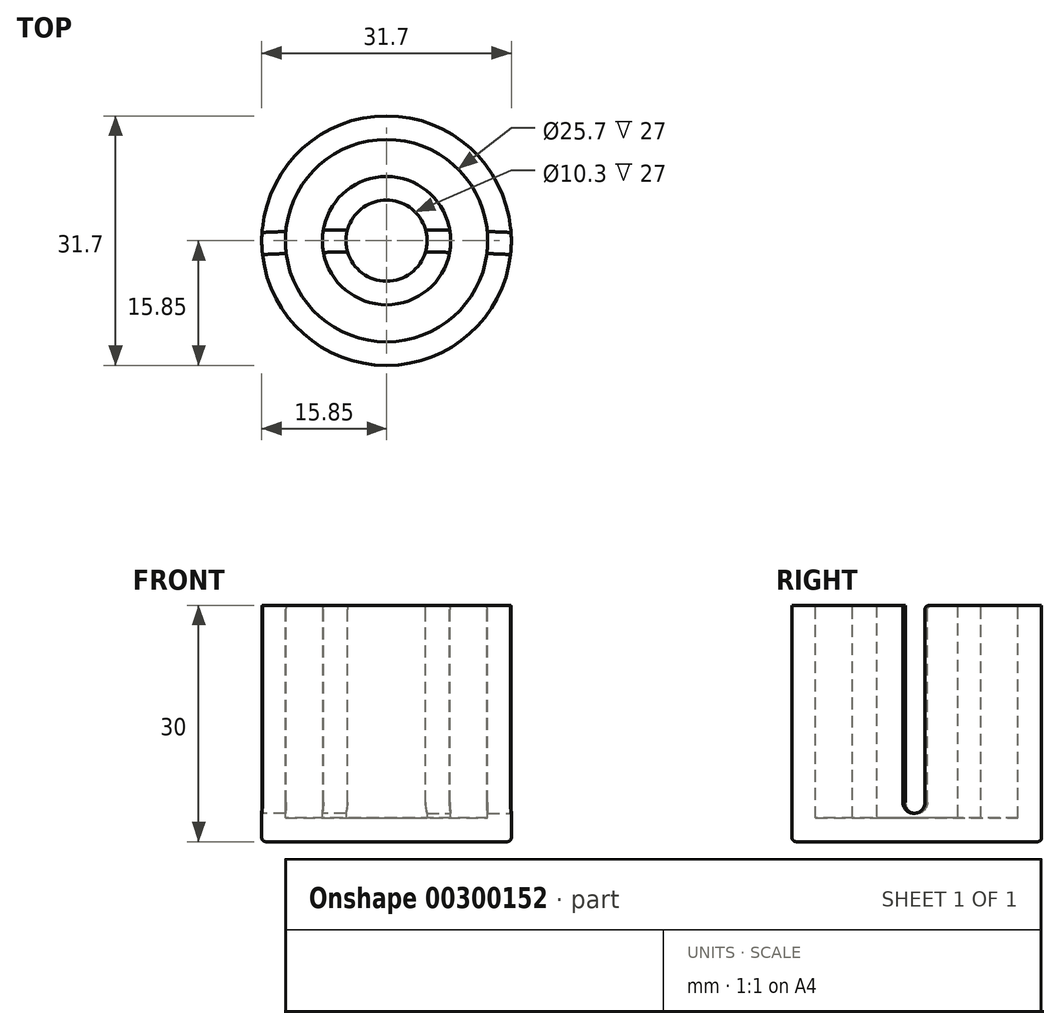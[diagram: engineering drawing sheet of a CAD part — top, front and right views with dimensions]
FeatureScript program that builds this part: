
annotation { "Feature Type Name" : "Feature", "Feature Type Description" : "" }
export const myFeature = defineFeature(function(context is Context, id is Id, definition is map)
    precondition{}
    {
        {
            var Q0;
            Q0=qCreatedBy(makeId("Top.planeOp"),FACE);
            var sketch = newSketch(context, id + "F0", { "sketchPlane" : qUnion([Q0])});
            skCircle(sketch, "E0", {"center": v(0, 0) * mm, "radius": 15.85 * mm});
            skCircle(sketch, "E1", {"center": v(0, 0) * mm, "radius": 5.15 * mm});
            skSolve(sketch);
        }
        {
            var Q0;
            Q0=qSketchRegion(id+"F0",true);
            extrude(context, id + "F1", {"entities" : qUnion([Q0]), "depth" : 30 * mm});
        }
        {
            var Q0;
            Q0=makeQuery(id+"F1.opExtrude","CAP_FACE",FACE,{"disambiguationData":[OSD([sQuery(id+"F0.wireOp",EDGE,"E0"),sQuery(id+"F0.wireOp",EDGE,"E1")])],"isStart":false});
            var sketch = newSketch(context, id + "F2", { "sketchPlane" : qUnion([Q0])});
            skCircle(sketch, "E2", {"center": v(0, 0) * mm, "radius": 12.85 * mm});
            skCircle(sketch, "E3", {"center": v(0, 0) * mm, "radius": 8.15 * mm});
            skSolve(sketch);
        }
        {
            var Q0;
            Q0=qSketchRegion(id+"F2",true);
            extrude(context, id + "F3", {"entities" : qUnion([Q0]), "operationType" : NewBodyOperationType.REMOVE, "oppositeDirection" : true, "depth" : 40 * mm});
        }
        {
            var Q0;
            Q0=makeQuery(id+"F1.opExtrude","CAP_FACE",FACE,{"disambiguationData":[OSD([sQuery(id+"F0.wireOp",EDGE,"E0"),sQuery(id+"F0.wireOp",EDGE,"E1")])],"isStart":true});
            var sketch = newSketch(context, id + "F4", { "sketchPlane" : qUnion([Q0])});
            skCircle(sketch, "E4", {"center": v(0, 0) * mm, "radius": 8.9 * mm});
            skCircle(sketch, "E5", {"center": v(0, 0) * mm, "radius": 12.65 * mm});
            skSolve(sketch);
        }
        {
            var Q0;
            Q0=qSketchRegion(id+"F4",true);
            extrude(context, id + "F5", {"entities" : qUnion([Q0]), "operationType" : NewBodyOperationType.REMOVE, "oppositeDirection" : true, "depth" : 40 * mm});
        }
        {
            var Q0;
            {var subQ0=sQuery(id+"F0.wireOp",EDGE,"E1");Q0=makeQuery(id+"F3.boolean.opBoolean","SPLIT",FACE,{"disambiguationData":[TD([makeQuery(id+"F1.opExtrude","SWEPT_FACE",FACE,{"disambiguationData":[OSD([subQ0])]})])],"derivedFrom":makeQuery(id+"F1.opExtrude","CAP_FACE",FACE,{"disambiguationData":[OSD([sQuery(id+"F0.wireOp",EDGE,"E0"),subQ0])],"isStart":false})});}
            var sketch = newSketch(context, id + "F6", { "sketchPlane" : qUnion([Q0])});
            skCircle(sketch, "E6", {"center": v(0, -340) * mm, "radius": 340 * mm, "construction": true});
            skPoint(sketch, "E7", {"position": v(0, 0) * mm});
            skSolve(sketch);
        }
        {
            var Q0;
            Q0=qCreatedBy(makeId("Right.planeOp"),FACE);
            var sketch = newSketch(context, id + "F7", { "sketchPlane" : qUnion([Q0])});
            skLineSegment(sketch, "E8", {"start": v(1.4, 30) * mm, "end": v(0, 30) * mm});
            skArc(sketch, "E9", {"start": v(0, 3.6) * mm, "mid": v(0.99, 4.01) * mm, "end": v(1.4, 5) * mm});
            skArc(sketch, "E10.MirrorCS", {"start": v(0, 3.6) * mm, "mid": v(-0.99, 4.01) * mm, "end": v(-1.4, 5) * mm});
            skLineSegment(sketch, "E11", {"start": v(0, 30) * mm, "end": v(-1.4, 30) * mm});
            skLineSegment(sketch, "E12", {"start": v(-1.4, 30) * mm, "end": v(-1.4, 5) * mm});
            skLineSegment(sketch, "E13", {"start": v(1.4, 5) * mm, "end": v(1.4, 30) * mm});
            skSolve(sketch);
        }
        {
            var Q0;
            Q0=qCreatedBy(makeId("Right.planeOp"),FACE);
            var sketch = newSketch(context, id + "F8", { "sketchPlane" : qUnion([Q0])});
            skLineSegment(sketch, "E14", {"start": v(-340, -124.57) * mm, "end": v(-340, 184) * mm, "construction": true});
            skSolve(sketch);
        }
        {
            var Q0;
            Q0=qSketchRegion(id+"F7",true);
            var Q1;
            Q1=sQuery(id+"F8.wireOp",EDGE,"E14");
            revolve(context, id + "F9", {"operationType" : NewBodyOperationType.REMOVE, "entities" : qUnion([Q0]), "axis" : qUnion([Q1]), "revolveType" : RevolveType.FULL, "oppositeDirection" : true});
        }
        {
            var Q0;
            {var subQ0=sQuery(id+"F0.wireOp",EDGE,"E0");Q0=makeQuery(id+"F9.boolean.opBoolean","SPLIT",EDGE,{"disambiguationData":[TD([makeQuery(id+"F9.opRevolve","SWEPT_FACE",FACE,{"disambiguationData":[OSD([sQuery(id+"F7.wireOp",EDGE,"EXb8YkG8-jNmO-N3WI-U9VX-eYOkCgfbIMvW")])]})])],"derivedFrom":makeQuery(id+"F1.opExtrude","CAP_EDGE",EDGE,{"disambiguationData":[OSD([subQ0])],"isStart":false})});}
            var Q1;
            {var subQ0=sQuery(id+"F2.wireOp",EDGE,"E2");Q1=makeQuery(id+"F9.boolean.opBoolean","SPLIT",EDGE,{"disambiguationData":[TD([makeQuery(id+"F9.opRevolve","SWEPT_FACE",FACE,{"disambiguationData":[OSD([sQuery(id+"F7.wireOp",EDGE,"EXb8YkG8-jNmO-N3WI-U9VX-eYOkCgfbIMvW")])]})])],"derivedFrom":makeQuery(id+"F3.boolean.opBoolean","COPY",EDGE,{"derivedFrom":makeQuery(id+"F3.opExtrude","CAP_EDGE",EDGE,{"disambiguationData":[OSD([subQ0])],"isStart":true})})});}
            var Q2;
            Q2=makeQuery(id+"F9.boolean.opBoolean","INTERSECT",EDGE,{"disambiguationData":[OD(0.0)],"derivedFrom":[makeQuery(id+"F1.opExtrude","SWEPT_FACE",FACE,{"disambiguationData":[OSD([sQuery(id+"F0.wireOp",EDGE,"E0")])]}),makeQuery(id+"F9.opRevolve","SWEPT_FACE",FACE,{"disambiguationData":[OSD([sQuery(id+"F7.wireOp",EDGE,"EXb8YkG8-jNmO-N3WI-U9VX-eYOkCgfbIMvW")])]})]});
            var Q3;
            {var subQ0=sQuery(id+"F0.wireOp",EDGE,"E0");var subQ1=sQuery(id+"F7.wireOp",EDGE,"EXb8YkG8-jNmO-N3WI-U9VX-eYOkCgfbIMvW");Q3=makeQuery(id+"F9.boolean.opBoolean","COPY",EDGE,{"disambiguationData":[TD([makeQuery(id+"F1.opExtrude","SWEPT_FACE",FACE,{"disambiguationData":[OSD([subQ0])]}),makeQuery(id+"F1.opExtrude","CAP_FACE",FACE,{"disambiguationData":[OSD([subQ0,sQuery(id+"F0.wireOp",EDGE,"E1")])],"isStart":false}),makeQuery(id+"F3.boolean.opBoolean","COPY",FACE,{"derivedFrom":makeQuery(id+"F3.opExtrude","SWEPT_FACE",FACE,{"disambiguationData":[OSD([sQuery(id+"F2.wireOp",EDGE,"E2")])]})}),makeQuery(id+"F9.opRevolve","SWEPT_FACE",FACE,{"disambiguationData":[OSD([subQ1])]})]),OD(0.0)],"derivedFrom":makeQuery(id+"F9.opRevolve","SWEPT_EDGE",EDGE,{"disambiguationData":[OSD([sQuery(id+"F7.wireOp",EDGE,"E8"),subQ1])]})});}
            var Q4;
            {var subQ0=sQuery(id+"F0.wireOp",EDGE,"E0");var subQ1=sQuery(id+"F7.wireOp",EDGE,"b1084e50-73aa-409a-998b-8d194c50b8df0.MirrorCS");Q4=makeQuery(id+"F9.boolean.opBoolean","COPY",EDGE,{"disambiguationData":[TD([makeQuery(id+"F1.opExtrude","SWEPT_FACE",FACE,{"disambiguationData":[OSD([subQ0])]}),makeQuery(id+"F1.opExtrude","CAP_FACE",FACE,{"disambiguationData":[OSD([subQ0,sQuery(id+"F0.wireOp",EDGE,"E1")])],"isStart":false}),makeQuery(id+"F3.boolean.opBoolean","COPY",FACE,{"derivedFrom":makeQuery(id+"F3.opExtrude","SWEPT_FACE",FACE,{"disambiguationData":[OSD([sQuery(id+"F2.wireOp",EDGE,"E2")])]})}),makeQuery(id+"F9.opRevolve","SWEPT_FACE",FACE,{"disambiguationData":[OSD([subQ1])]})]),OD(0.0)],"derivedFrom":makeQuery(id+"F9.opRevolve","SWEPT_EDGE",EDGE,{"disambiguationData":[OSD([subQ1,sQuery(id+"F7.wireOp",EDGE,"E11")])]})});}
            var Q5;
            {var subQ0=sQuery(id+"F0.wireOp",EDGE,"E0");Q5=makeQuery(id+"F9.boolean.opBoolean","SPLIT",EDGE,{"disambiguationData":[TD([makeQuery(id+"F9.opRevolve","SWEPT_FACE",FACE,{"disambiguationData":[OSD([sQuery(id+"F7.wireOp",EDGE,"b1084e50-73aa-409a-998b-8d194c50b8df0.MirrorCS")])]})])],"derivedFrom":makeQuery(id+"F1.opExtrude","CAP_EDGE",EDGE,{"disambiguationData":[OSD([subQ0])],"isStart":false})});}
            var Q6;
            {var subQ0=sQuery(id+"F2.wireOp",EDGE,"E2");Q6=makeQuery(id+"F9.boolean.opBoolean","SPLIT",EDGE,{"disambiguationData":[TD([makeQuery(id+"F9.opRevolve","SWEPT_FACE",FACE,{"disambiguationData":[OSD([sQuery(id+"F7.wireOp",EDGE,"b1084e50-73aa-409a-998b-8d194c50b8df0.MirrorCS")])]})])],"derivedFrom":makeQuery(id+"F3.boolean.opBoolean","COPY",EDGE,{"derivedFrom":makeQuery(id+"F3.opExtrude","CAP_EDGE",EDGE,{"disambiguationData":[OSD([subQ0])],"isStart":true})})});}
            var Q7;
            Q7=makeQuery(id+"F9.boolean.opBoolean","INTERSECT",EDGE,{"disambiguationData":[OD(0.0)],"derivedFrom":[makeQuery(id+"F3.boolean.opBoolean","COPY",FACE,{"derivedFrom":makeQuery(id+"F3.opExtrude","SWEPT_FACE",FACE,{"disambiguationData":[OSD([sQuery(id+"F2.wireOp",EDGE,"E2")])]})}),makeQuery(id+"F9.opRevolve","SWEPT_FACE",FACE,{"disambiguationData":[OSD([sQuery(id+"F7.wireOp",EDGE,"EXb8YkG8-jNmO-N3WI-U9VX-eYOkCgfbIMvW")])]})]});
            var Q8;
            Q8=makeQuery(id+"F9.boolean.opBoolean","INTERSECT",EDGE,{"disambiguationData":[OD(1.0)],"derivedFrom":[makeQuery(id+"F1.opExtrude","SWEPT_FACE",FACE,{"disambiguationData":[OSD([sQuery(id+"F0.wireOp",EDGE,"E0")])]}),makeQuery(id+"F9.opRevolve","SWEPT_FACE",FACE,{"disambiguationData":[OSD([sQuery(id+"F7.wireOp",EDGE,"EXb8YkG8-jNmO-N3WI-U9VX-eYOkCgfbIMvW")])]})]});
            var Q9;
            Q9=makeQuery(id+"F9.boolean.opBoolean","INTERSECT",EDGE,{"disambiguationData":[OD(1.0)],"derivedFrom":[makeQuery(id+"F3.boolean.opBoolean","COPY",FACE,{"derivedFrom":makeQuery(id+"F3.opExtrude","SWEPT_FACE",FACE,{"disambiguationData":[OSD([sQuery(id+"F2.wireOp",EDGE,"E2")])]})}),makeQuery(id+"F9.opRevolve","SWEPT_FACE",FACE,{"disambiguationData":[OSD([sQuery(id+"F7.wireOp",EDGE,"EXb8YkG8-jNmO-N3WI-U9VX-eYOkCgfbIMvW")])]})]});
            var Q10;
            {var subQ0=sQuery(id+"F0.wireOp",EDGE,"E0");var subQ1=sQuery(id+"F7.wireOp",EDGE,"EXb8YkG8-jNmO-N3WI-U9VX-eYOkCgfbIMvW");Q10=makeQuery(id+"F9.boolean.opBoolean","COPY",EDGE,{"disambiguationData":[TD([makeQuery(id+"F1.opExtrude","SWEPT_FACE",FACE,{"disambiguationData":[OSD([subQ0])]}),makeQuery(id+"F1.opExtrude","CAP_FACE",FACE,{"disambiguationData":[OSD([subQ0,sQuery(id+"F0.wireOp",EDGE,"E1")])],"isStart":false}),makeQuery(id+"F3.boolean.opBoolean","COPY",FACE,{"derivedFrom":makeQuery(id+"F3.opExtrude","SWEPT_FACE",FACE,{"disambiguationData":[OSD([sQuery(id+"F2.wireOp",EDGE,"E2")])]})}),makeQuery(id+"F9.opRevolve","SWEPT_FACE",FACE,{"disambiguationData":[OSD([subQ1])]})]),OD(1.0)],"derivedFrom":makeQuery(id+"F9.opRevolve","SWEPT_EDGE",EDGE,{"disambiguationData":[OSD([sQuery(id+"F7.wireOp",EDGE,"E8"),subQ1])]})});}
            var Q11;
            {var subQ0=sQuery(id+"F0.wireOp",EDGE,"E0");var subQ1=sQuery(id+"F7.wireOp",EDGE,"b1084e50-73aa-409a-998b-8d194c50b8df0.MirrorCS");Q11=makeQuery(id+"F9.boolean.opBoolean","COPY",EDGE,{"disambiguationData":[TD([makeQuery(id+"F1.opExtrude","SWEPT_FACE",FACE,{"disambiguationData":[OSD([subQ0])]}),makeQuery(id+"F1.opExtrude","CAP_FACE",FACE,{"disambiguationData":[OSD([subQ0,sQuery(id+"F0.wireOp",EDGE,"E1")])],"isStart":false}),makeQuery(id+"F3.boolean.opBoolean","COPY",FACE,{"derivedFrom":makeQuery(id+"F3.opExtrude","SWEPT_FACE",FACE,{"disambiguationData":[OSD([sQuery(id+"F2.wireOp",EDGE,"E2")])]})}),makeQuery(id+"F9.opRevolve","SWEPT_FACE",FACE,{"disambiguationData":[OSD([subQ1])]})]),OD(1.0)],"derivedFrom":makeQuery(id+"F9.opRevolve","SWEPT_EDGE",EDGE,{"disambiguationData":[OSD([subQ1,sQuery(id+"F7.wireOp",EDGE,"E11")])]})});}
            var Q12;
            {var subQ0=sQuery(id+"F2.wireOp",EDGE,"E3");Q12=makeQuery(id+"F9.boolean.opBoolean","SPLIT",EDGE,{"disambiguationData":[TD([makeQuery(id+"F9.opRevolve","SWEPT_FACE",FACE,{"disambiguationData":[OSD([sQuery(id+"F7.wireOp",EDGE,"b1084e50-73aa-409a-998b-8d194c50b8df0.MirrorCS")])]})])],"derivedFrom":makeQuery(id+"F3.boolean.opBoolean","COPY",EDGE,{"derivedFrom":makeQuery(id+"F3.opExtrude","CAP_EDGE",EDGE,{"disambiguationData":[OSD([subQ0])],"isStart":true})})});}
            var Q13;
            {var subQ0=sQuery(id+"F0.wireOp",EDGE,"E1");var subQ1=sQuery(id+"F7.wireOp",EDGE,"b1084e50-73aa-409a-998b-8d194c50b8df0.MirrorCS");Q13=makeQuery(id+"F9.boolean.opBoolean","COPY",EDGE,{"disambiguationData":[TD([makeQuery(id+"F1.opExtrude","CAP_FACE",FACE,{"disambiguationData":[OSD([sQuery(id+"F0.wireOp",EDGE,"E0"),subQ0])],"isStart":false}),makeQuery(id+"F1.opExtrude","SWEPT_FACE",FACE,{"disambiguationData":[OSD([subQ0])]}),makeQuery(id+"F3.boolean.opBoolean","COPY",FACE,{"derivedFrom":makeQuery(id+"F3.opExtrude","SWEPT_FACE",FACE,{"disambiguationData":[OSD([sQuery(id+"F2.wireOp",EDGE,"E3")])]})}),makeQuery(id+"F9.opRevolve","SWEPT_FACE",FACE,{"disambiguationData":[OSD([subQ1])]})]),OD(1.0)],"derivedFrom":makeQuery(id+"F9.opRevolve","SWEPT_EDGE",EDGE,{"disambiguationData":[OSD([subQ1,sQuery(id+"F7.wireOp",EDGE,"E11")])]})});}
            var Q14;
            {var subQ0=sQuery(id+"F0.wireOp",EDGE,"E1");var subQ1=sQuery(id+"F7.wireOp",EDGE,"EXb8YkG8-jNmO-N3WI-U9VX-eYOkCgfbIMvW");Q14=makeQuery(id+"F9.boolean.opBoolean","COPY",EDGE,{"disambiguationData":[TD([makeQuery(id+"F1.opExtrude","CAP_FACE",FACE,{"disambiguationData":[OSD([sQuery(id+"F0.wireOp",EDGE,"E0"),subQ0])],"isStart":false}),makeQuery(id+"F1.opExtrude","SWEPT_FACE",FACE,{"disambiguationData":[OSD([subQ0])]}),makeQuery(id+"F3.boolean.opBoolean","COPY",FACE,{"derivedFrom":makeQuery(id+"F3.opExtrude","SWEPT_FACE",FACE,{"disambiguationData":[OSD([sQuery(id+"F2.wireOp",EDGE,"E3")])]})}),makeQuery(id+"F9.opRevolve","SWEPT_FACE",FACE,{"disambiguationData":[OSD([subQ1])]})]),OD(1.0)],"derivedFrom":makeQuery(id+"F9.opRevolve","SWEPT_EDGE",EDGE,{"disambiguationData":[OSD([sQuery(id+"F7.wireOp",EDGE,"E8"),subQ1])]})});}
            var Q15;
            {var subQ0=sQuery(id+"F2.wireOp",EDGE,"E3");Q15=makeQuery(id+"F9.boolean.opBoolean","SPLIT",EDGE,{"disambiguationData":[TD([makeQuery(id+"F9.opRevolve","SWEPT_FACE",FACE,{"disambiguationData":[OSD([sQuery(id+"F7.wireOp",EDGE,"EXb8YkG8-jNmO-N3WI-U9VX-eYOkCgfbIMvW")])]})])],"derivedFrom":makeQuery(id+"F3.boolean.opBoolean","COPY",EDGE,{"derivedFrom":makeQuery(id+"F3.opExtrude","CAP_EDGE",EDGE,{"disambiguationData":[OSD([subQ0])],"isStart":true})})});}
            var Q16;
            {var subQ0=sQuery(id+"F0.wireOp",EDGE,"E1");var subQ1=sQuery(id+"F7.wireOp",EDGE,"EXb8YkG8-jNmO-N3WI-U9VX-eYOkCgfbIMvW");Q16=makeQuery(id+"F9.boolean.opBoolean","COPY",EDGE,{"disambiguationData":[TD([makeQuery(id+"F1.opExtrude","CAP_FACE",FACE,{"disambiguationData":[OSD([sQuery(id+"F0.wireOp",EDGE,"E0"),subQ0])],"isStart":false}),makeQuery(id+"F1.opExtrude","SWEPT_FACE",FACE,{"disambiguationData":[OSD([subQ0])]}),makeQuery(id+"F3.boolean.opBoolean","COPY",FACE,{"derivedFrom":makeQuery(id+"F3.opExtrude","SWEPT_FACE",FACE,{"disambiguationData":[OSD([sQuery(id+"F2.wireOp",EDGE,"E3")])]})}),makeQuery(id+"F9.opRevolve","SWEPT_FACE",FACE,{"disambiguationData":[OSD([subQ1])]})]),OD(0.0)],"derivedFrom":makeQuery(id+"F9.opRevolve","SWEPT_EDGE",EDGE,{"disambiguationData":[OSD([sQuery(id+"F7.wireOp",EDGE,"E8"),subQ1])]})});}
            var Q17;
            {var subQ0=sQuery(id+"F0.wireOp",EDGE,"E1");var subQ1=sQuery(id+"F7.wireOp",EDGE,"b1084e50-73aa-409a-998b-8d194c50b8df0.MirrorCS");Q17=makeQuery(id+"F9.boolean.opBoolean","COPY",EDGE,{"disambiguationData":[TD([makeQuery(id+"F1.opExtrude","CAP_FACE",FACE,{"disambiguationData":[OSD([sQuery(id+"F0.wireOp",EDGE,"E0"),subQ0])],"isStart":false}),makeQuery(id+"F1.opExtrude","SWEPT_FACE",FACE,{"disambiguationData":[OSD([subQ0])]}),makeQuery(id+"F3.boolean.opBoolean","COPY",FACE,{"derivedFrom":makeQuery(id+"F3.opExtrude","SWEPT_FACE",FACE,{"disambiguationData":[OSD([sQuery(id+"F2.wireOp",EDGE,"E3")])]})}),makeQuery(id+"F9.opRevolve","SWEPT_FACE",FACE,{"disambiguationData":[OSD([subQ1])]})]),OD(0.0)],"derivedFrom":makeQuery(id+"F9.opRevolve","SWEPT_EDGE",EDGE,{"disambiguationData":[OSD([subQ1,sQuery(id+"F7.wireOp",EDGE,"E11")])]})});}
            var Q18;
            {var subQ0=sQuery(id+"F0.wireOp",EDGE,"E1");Q18=makeQuery(id+"F9.boolean.opBoolean","SPLIT",EDGE,{"disambiguationData":[TD([makeQuery(id+"F9.opRevolve","SWEPT_FACE",FACE,{"disambiguationData":[OSD([sQuery(id+"F7.wireOp",EDGE,"b1084e50-73aa-409a-998b-8d194c50b8df0.MirrorCS")])]})])],"derivedFrom":makeQuery(id+"F1.opExtrude","CAP_EDGE",EDGE,{"disambiguationData":[OSD([subQ0])],"isStart":false})});}
            var Q19;
            {var subQ0=sQuery(id+"F0.wireOp",EDGE,"E1");Q19=makeQuery(id+"F9.boolean.opBoolean","SPLIT",EDGE,{"disambiguationData":[TD([makeQuery(id+"F9.opRevolve","SWEPT_FACE",FACE,{"disambiguationData":[OSD([sQuery(id+"F7.wireOp",EDGE,"EXb8YkG8-jNmO-N3WI-U9VX-eYOkCgfbIMvW")])]})])],"derivedFrom":makeQuery(id+"F1.opExtrude","CAP_EDGE",EDGE,{"disambiguationData":[OSD([subQ0])],"isStart":false})});}
            var Q20;
            Q20=makeQuery(id+"F1.opExtrude","CAP_EDGE",EDGE,{"disambiguationData":[OSD([sQuery(id+"F0.wireOp",EDGE,"E0")])],"isStart":true});
            var Q21;
            Q21=makeQuery(id+"F5.boolean.opBoolean","COPY",EDGE,{"derivedFrom":makeQuery(id+"F5.opExtrude","CAP_EDGE",EDGE,{"disambiguationData":[OSD([sQuery(id+"F4.wireOp",EDGE,"E5")])],"isStart":true})});
            var Q22;
            Q22=makeQuery(id+"F5.boolean.opBoolean","COPY",EDGE,{"derivedFrom":makeQuery(id+"F5.opExtrude","CAP_EDGE",EDGE,{"disambiguationData":[OSD([sQuery(id+"F4.wireOp",EDGE,"E4")])],"isStart":true})});
            var Q23;
            Q23=makeQuery(id+"F1.opExtrude","CAP_EDGE",EDGE,{"disambiguationData":[OSD([sQuery(id+"F0.wireOp",EDGE,"E1")])],"isStart":true});
            fillet(context, id + "F10", {"entities" : qUnion([Q0, Q1, Q2, Q3, Q4, Q5, Q6, Q7, Q8, Q9, Q10, Q11, Q12, Q13, Q14, Q15, Q16, Q17, Q18, Q19, Q20, Q21, Q22, Q23]), "radius" : 0.5 * mm, "tangentPropagation" : true, "allowEdgeOverflow" : false});
        }
        {
            var Q0;
            {var subQ0=sQuery(id+"F0.wireOp",EDGE,"E0");Q0=makeQuery(id+"F3.boolean.opBoolean","SPLIT",FACE,{"disambiguationData":[TD([makeQuery(id+"F1.opExtrude","SWEPT_FACE",FACE,{"disambiguationData":[OSD([subQ0])]})])],"derivedFrom":makeQuery(id+"F1.opExtrude","CAP_FACE",FACE,{"disambiguationData":[OSD([subQ0,sQuery(id+"F0.wireOp",EDGE,"E1")])],"isStart":true})});}
            var sketch = newSketch(context, id + "F11", { "sketchPlane" : qUnion([Q0])});
            skCircle(sketch, "E15", {"center": v(0, 0) * mm, "radius": 15.35 * mm});
            skSolve(sketch);
        }
        {
            var Q0;
            Q0 = qSketchRegion(id + "F11", true);
            extrude(context, id + "F12", {"entities" : qUnion([Q0]), "operationType" : NewBodyOperationType.ADD, "oppositeDirection" : true, "depth" : 3 * mm});
        }
    });
